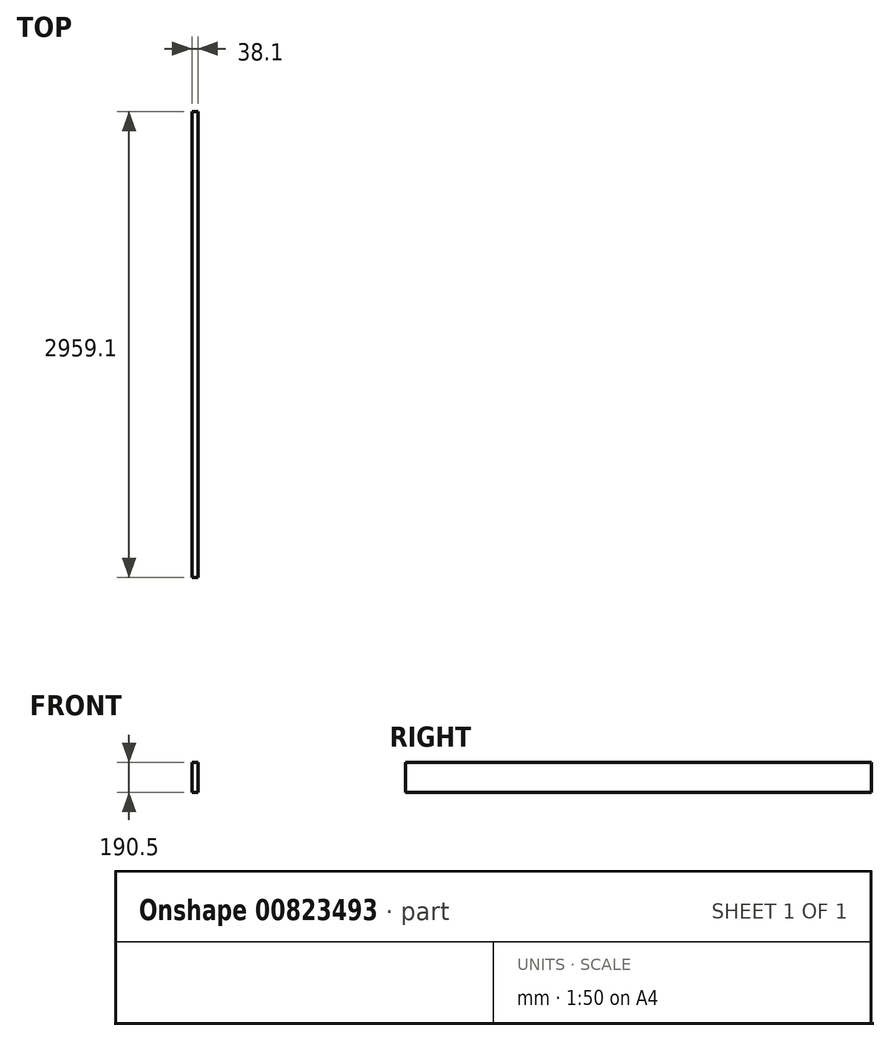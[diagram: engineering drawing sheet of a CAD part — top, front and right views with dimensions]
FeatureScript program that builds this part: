
annotation { "Feature Type Name" : "Feature", "Feature Type Description" : "" }
export const myFeature = defineFeature(function(context is Context, id is Id, definition is map)
    precondition{}
    {
        {
            var Q0;
            Q0=qCreatedBy(makeId("Front.planeOp"),FACE);
            var sketch = newSketch(context, id + "F0", { "sketchPlane" : qUnion([Q0])});
            skLineSegment(sketch, "E0.bottom", {"start": v(0, 0) * mm, "end": v(38.1, 0) * mm});
            skLineSegment(sketch, "E0.top", {"start": v(0, 190.5) * mm, "end": v(38.1, 190.5) * mm});
            skLineSegment(sketch, "E0.left", {"start": v(0, 0) * mm, "end": v(0, 190.5) * mm});
            skLineSegment(sketch, "E0.right", {"start": v(38.1, 0) * mm, "end": v(38.1, 190.5) * mm});
            skSolve(sketch);
        }
        {
            var Q0;
            Q0=qSketchRegion(id+"F0",true);
            extrude(context, id + "F1", {"entities" : qUnion([Q0]), "depth" : 2959.1 * mm, "offsetDistance" : 25.4 * mm});
        }
    });
